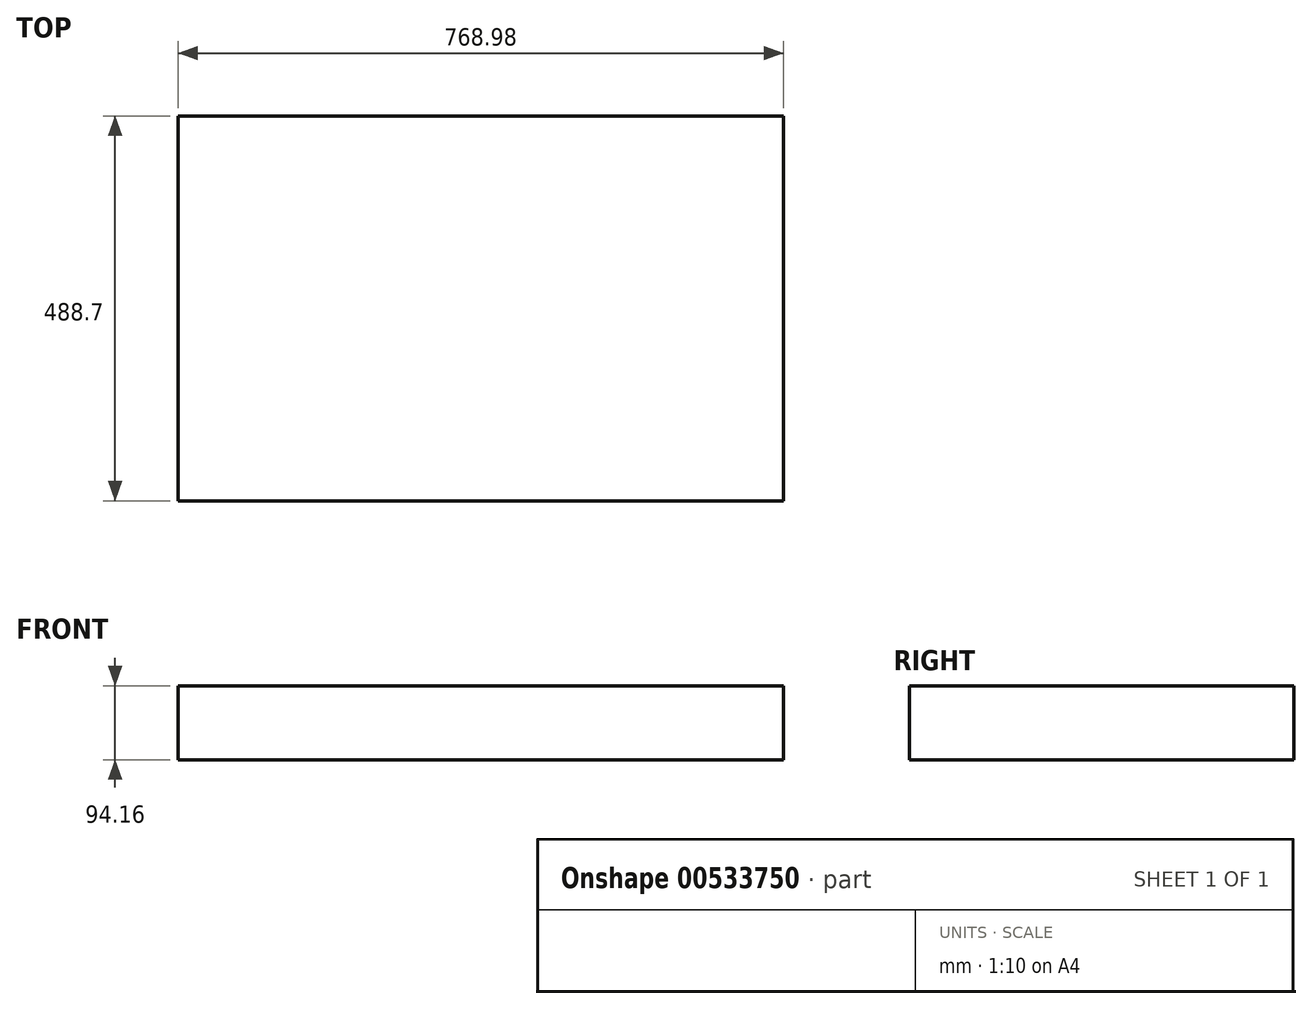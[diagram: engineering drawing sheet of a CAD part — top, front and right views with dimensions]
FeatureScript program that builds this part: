
annotation { "Feature Type Name" : "Feature", "Feature Type Description" : "" }
export const myFeature = defineFeature(function(context is Context, id is Id, definition is map)
    precondition{}
    {
        {
            var Q0;
            Q0=qCreatedBy(makeId("Top.planeOp"),FACE);
            var sketch = newSketch(context, id + "F0", { "sketchPlane" : qUnion([Q0])});
            skLineSegment(sketch, "E0.bottom", {"start": v(384.5, 244.35) * mm, "end": v(-384.5, 244.35) * mm});
            skLineSegment(sketch, "E0.top", {"start": v(384.5, -244.35) * mm, "end": v(-384.5, -244.35) * mm});
            skLineSegment(sketch, "E0.left", {"start": v(384.5, 244.35) * mm, "end": v(384.5, -244.35) * mm});
            skLineSegment(sketch, "E0.right", {"start": v(-384.5, 244.35) * mm, "end": v(-384.5, -244.35) * mm});
            skPoint(sketch, "E0.middle", {"position": v(0, 0) * mm});
            skSolve(sketch);
        }
        {
            var Q0;
            Q0=makeQuery(id+"F0.imprint","IMPRINT",FACE,{"disambiguationData":[TD([[makeQuery(id+"F0.imprint","IMPRINT",EDGE,{"derivedFrom":sQuery(id+"F0.wireOp",EDGE,"E0.bottom")}),1.0]])]});
            extrude(context, id + "F1", {"entities" : qUnion([Q0]), "depth" : 94.16 * mm, "offsetDistance" : 25.4 * mm});
        }
    });
